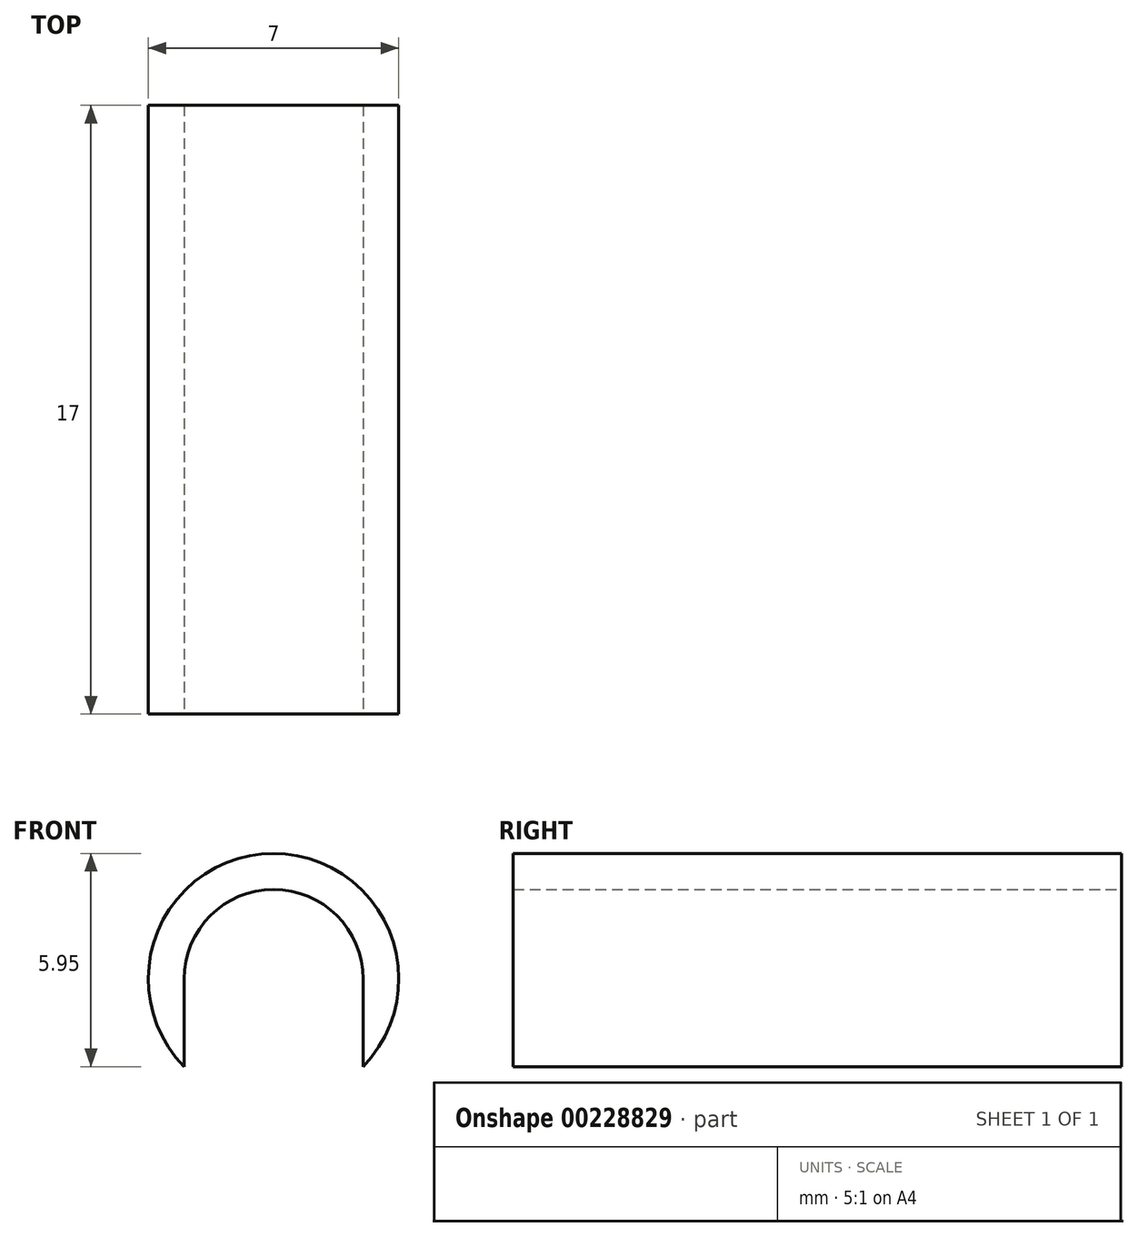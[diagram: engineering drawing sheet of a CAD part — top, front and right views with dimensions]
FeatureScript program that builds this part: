
annotation { "Feature Type Name" : "Feature", "Feature Type Description" : "" }
export const myFeature = defineFeature(function(context is Context, id is Id, definition is map)
    precondition{}
    {
        {
            var Q0;
            Q0=qCreatedBy(makeId("Front.planeOp"),FACE);
            var sketch = newSketch(context, id + "F0", { "sketchPlane" : qUnion([Q0])});
            skCircle(sketch, "E0", {"center": v(0, 0) * mm, "radius": 2.5 * mm});
            skCircle(sketch, "E1", {"center": v(0, 0) * mm, "radius": 3.5 * mm});
            skSolve(sketch);
        }
        {
            var Q0;
            Q0=makeQuery(id+"F0.imprint","IMPRINT",FACE,{"disambiguationData":[TD([[makeQuery(id+"F0.imprint","IMPRINT",EDGE,{"derivedFrom":sQuery(id+"F0.wireOp",EDGE,"E0")}),-1.0]])]});
            extrude(context, id + "F1", {"entities" : qUnion([Q0]), "depth" : ((17 / 2)) * mm, "hasSecondDirection" : true, "secondDirectionOppositeDirection" : true, "secondDirectionDepth" : ((17 / 2)) * mm});
        }
        {
            var Q0;
            Q0=makeQuery(id+"F1.opExtrude","CAP_FACE",FACE,{"disambiguationData":[OSD([sQuery(id+"F0.wireOp",EDGE,"E0"),sQuery(id+"F0.wireOp",EDGE,"E1")])],"isStart":false});
            var sketch = newSketch(context, id + "F2", { "sketchPlane" : qUnion([Q0])});
            skLineSegment(sketch, "E2.bottom", {"start": v(-2.5, 0) * mm, "end": v(2.5, 0) * mm});
            skLineSegment(sketch, "E2.top", {"start": v(-2.5, -3.5) * mm, "end": v(2.5, -3.5) * mm});
            skLineSegment(sketch, "E2.left", {"start": v(-2.5, 0) * mm, "end": v(-2.5, -3.5) * mm});
            skLineSegment(sketch, "E2.right", {"start": v(2.5, 0) * mm, "end": v(2.5, -3.5) * mm});
            skSolve(sketch);
        }
        {
            var Q0;
            {var subQ0=sQuery(id+"F2.wireOp",EDGE,"E2.bottom");Q0=makeQuery(id+"F2.imprint","IMPRINT",FACE,{"disambiguationData":[TD([[makeQuery(id+"F2.imprint","IMPRINT",EDGE,{"derivedFrom":subQ0}),-1.0]])]});}
            var Q1;
            {var subQ0=sQuery(id+"F2.wireOp",EDGE,"E2.left");var subQ1=sQuery(id+"F2.wireOp",EDGE,"E2.top");var subQ2=makeQuery(id+"F2.imprint","INTERSECT",VERTEX,{"derivedFrom":[subQ1,subQ0]});Q1=makeQuery(id+"F2.imprint","IMPRINT",FACE,{"disambiguationData":[TD([[makeQuery(id+"F2.imprint","IMPRINT",EDGE,{"disambiguationData":[TD([[subQ2,-1.0]])],"derivedFrom":subQ1}),1.0]])]});}
            var Q2;
            {var subQ4=makeQuery(id+"F1.opExtrude","CAP_EDGE",EDGE,{"disambiguationData":[OSD([sQuery(id+"F0.wireOp",EDGE,"E1")])],"isStart":false});var subQ6=makeQuery(id+"F2.imprint","INTERSECT",VERTEX,{"derivedFrom":[subQ4,sQuery(id+"F2.wireOp",EDGE,"E2.top")]});Q2=makeQuery(id+"F2.imprint","IMPRINT",FACE,{"disambiguationData":[TD([[makeQuery(id+"F2.imprint","IMPRINT",EDGE,{"disambiguationData":[TD([[subQ6,1.0]])],"derivedFrom":subQ4}),1.0]])]});}
            var Q3;
            {var subQ0=sQuery(id+"F2.wireOp",EDGE,"E2.right");var subQ1=sQuery(id+"F2.wireOp",EDGE,"E2.top");var subQ2=makeQuery(id+"F2.imprint","INTERSECT",VERTEX,{"derivedFrom":[subQ1,subQ0]});Q3=makeQuery(id+"F2.imprint","IMPRINT",FACE,{"disambiguationData":[TD([[makeQuery(id+"F2.imprint","IMPRINT",EDGE,{"disambiguationData":[TD([[subQ2,1.0]])],"derivedFrom":subQ1}),1.0]])]});}
            extrude(context, id + "F3", {"entities" : qUnion([Q0, Q1, Q2, Q3]), "operationType" : NewBodyOperationType.REMOVE, "endBound" : BoundingType.THROUGH_ALL, "oppositeDirection" : true, "depth" : 25 * mm});
        }
    });
